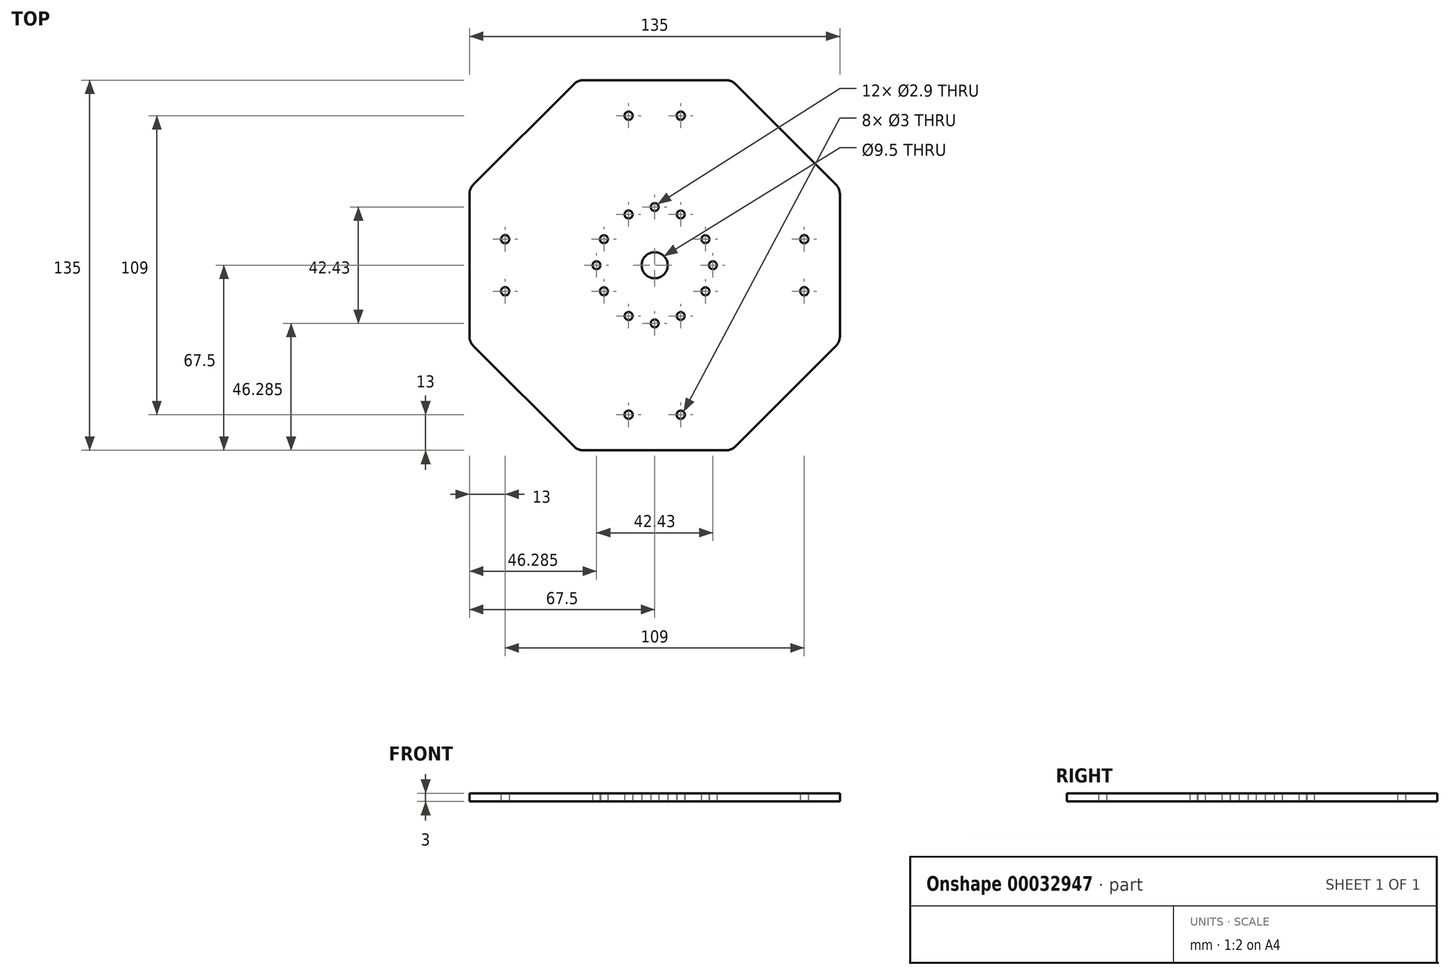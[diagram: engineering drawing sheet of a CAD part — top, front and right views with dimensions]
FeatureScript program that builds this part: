
annotation { "Feature Type Name" : "Feature", "Feature Type Description" : "" }
export const myFeature = defineFeature(function(context is Context, id is Id, definition is map)
    precondition{}
    {
        {
            var Q0;
            Q0=qCreatedBy(makeId("Top.planeOp"),FACE);
            var sketch = newSketch(context, id + "F0", { "sketchPlane" : qUnion([Q0])});
            skPoint(sketch, "E0.rect.middle", {"position": v(0, 0) * mm});
            skLineSegment(sketch, "E1", {"start": v(0, 67.5) * mm, "end": v(0, -67.5) * mm, "construction": true});
            skLineSegment(sketch, "E2", {"start": v(-67.5, 0) * mm, "end": v(67.5, 0) * mm, "construction": true});
            skLineSegment(sketch, "E3.rect.bottom", {"start": v(14, -14) * mm, "end": v(-14, -14) * mm, "construction": true});
            skLineSegment(sketch, "E3.rect.top", {"start": v(14, 14) * mm, "end": v(-14, 14) * mm, "construction": true});
            skLineSegment(sketch, "E3.rect.left", {"start": v(14, -14) * mm, "end": v(14, 14) * mm, "construction": true});
            skLineSegment(sketch, "E3.rect.right", {"start": v(-14, -14) * mm, "end": v(-14, 14) * mm, "construction": true});
            skLineSegment(sketch, "E4.rect.bottom", {"start": v(5, -5) * mm, "end": v(-5, -5) * mm, "construction": true});
            skLineSegment(sketch, "E4.rect.top", {"start": v(5, 5) * mm, "end": v(-5, 5) * mm, "construction": true});
            skLineSegment(sketch, "E4.rect.left", {"start": v(5, -5) * mm, "end": v(5, 5) * mm, "construction": true});
            skLineSegment(sketch, "E4.rect.right", {"start": v(-5, -5) * mm, "end": v(-5, 5) * mm, "construction": true});
            skLineSegment(sketch, "E5.bottom", {"start": v(-14, 14) * mm, "end": v(14, 14) * mm, "construction": true});
            skLineSegment(sketch, "E5.top", {"start": v(-14, 23) * mm, "end": v(14, 23) * mm, "construction": true});
            skLineSegment(sketch, "E5.left", {"start": v(-14, 14) * mm, "end": v(-14, 23) * mm, "construction": true});
            skLineSegment(sketch, "E5.right", {"start": v(14, 14) * mm, "end": v(14, 23) * mm, "construction": true});
            skLineSegment(sketch, "E6", {"start": v(5, 23) * mm, "end": v(5, 14) * mm, "construction": true});
            skLineSegment(sketch, "E7", {"start": v(14, 18.5) * mm, "end": v(5, 18.5) * mm, "construction": true});
            skCircle(sketch, "E8", {"center": v(9.5, 18.5) * mm, "radius": 1.45 * mm});
            skCircle(sketch, "E9.MirrorC", {"center": v(-9.5, 18.5) * mm, "radius": 1.45 * mm});
            skCircle(sketch, "E10.MirrorC", {"center": v(-9.5, -18.5) * mm, "radius": 1.45 * mm});
            skCircle(sketch, "E11.MirrorC", {"center": v(9.5, -18.5) * mm, "radius": 1.45 * mm});
            skCircle(sketch, "E12", {"center": v(0, 0) * mm, "radius": 20.8 * mm, "construction": true});
            skLineSegment(sketch, "E13", {"start": v(0, 0) * mm, "end": v(14, 14) * mm, "construction": true});
            skCircle(sketch, "E14.MirrorC", {"center": v(18.5, -9.5) * mm, "radius": 1.45 * mm});
            skCircle(sketch, "E15.MirrorC", {"center": v(18.5, 9.5) * mm, "radius": 1.45 * mm});
            skLineSegment(sketch, "E16", {"start": v(0, 0) * mm, "end": v(-14, 14) * mm, "construction": true});
            skCircle(sketch, "E17.MirrorC", {"center": v(-18.5, 9.5) * mm, "radius": 1.45 * mm});
            skCircle(sketch, "E18.MirrorC", {"center": v(-18.5, -9.5) * mm, "radius": 1.45 * mm});
            skCircle(sketch, "E19", {"center": v(9.5, 54.5) * mm, "radius": 1.5 * mm});
            skCircle(sketch, "E20.MirrorC", {"center": v(-9.5, 54.5) * mm, "radius": 1.5 * mm});
            skCircle(sketch, "E21.MirrorC", {"center": v(-9.5, -54.5) * mm, "radius": 1.5 * mm});
            skCircle(sketch, "E22.MirrorC", {"center": v(9.5, -54.5) * mm, "radius": 1.5 * mm});
            skCircle(sketch, "E23.MirrorC", {"center": v(54.5, -9.5) * mm, "radius": 1.5 * mm});
            skCircle(sketch, "E24.MirrorC", {"center": v(54.5, 9.5) * mm, "radius": 1.5 * mm});
            skCircle(sketch, "E25.MirrorC", {"center": v(-54.5, -9.5) * mm, "radius": 1.5 * mm});
            skCircle(sketch, "E26.MirrorC", {"center": v(-54.5, 9.5) * mm, "radius": 1.5 * mm});
            skLineSegment(sketch, "E27", {"start": v(0, 0) * mm, "end": v(95.46, 0) * mm, "construction": true});
            skLineSegment(sketch, "E28.MirrorCS", {"start": v(0, 0) * mm, "end": v(0, 95.46) * mm, "construction": true});
            skLineSegment(sketch, "E29", {"start": v(27.96, 67.5) * mm, "end": v(67.5, 27.96) * mm});
            skLineSegment(sketch, "E30.MirrorCS", {"start": v(-67.5, -27.96) * mm, "end": v(-27.96, -67.5) * mm});
            skLineSegment(sketch, "E31.MirrorCS", {"start": v(-27.96, 67.5) * mm, "end": v(-67.5, 27.96) * mm});
            skLineSegment(sketch, "E32.MirrorCS", {"start": v(27.96, -67.5) * mm, "end": v(67.5, -27.96) * mm});
            skLineSegment(sketch, "E33", {"start": v(67.5, -27.96) * mm, "end": v(67.5, 27.96) * mm});
            skLineSegment(sketch, "E34.MirrorCS", {"start": v(-67.5, -27.96) * mm, "end": v(-67.5, 27.96) * mm});
            skLineSegment(sketch, "E35.MirrorCS", {"start": v(-27.96, 67.5) * mm, "end": v(27.96, 67.5) * mm});
            skLineSegment(sketch, "E36.MirrorCS", {"start": v(27.96, -67.5) * mm, "end": v(-27.96, -67.5) * mm});
            skPoint(sketch, "E37.orphan", {"position": v(0, 95.46) * mm});
            skPoint(sketch, "E38.orphan", {"position": v(95.46, 0) * mm});
            skPoint(sketch, "E39.orphan", {"position": v(0, -95.46) * mm});
            skPoint(sketch, "E40.orphan", {"position": v(-95.46, 0) * mm});
            skCircle(sketch, "E41", {"center": v(0, 0) * mm, "radius": 4.75 * mm});
            skCircle(sketch, "E42", {"center": v(0, 21.21) * mm, "radius": 1.45 * mm});
            skCircle(sketch, "E43.1.0", {"center": v(-21.21, 0) * mm, "radius": 1.45 * mm});
            skCircle(sketch, "E43.2.0", {"center": v(0, -21.21) * mm, "radius": 1.45 * mm});
            skCircle(sketch, "E43.3.0", {"center": v(21.21, 0) * mm, "radius": 1.45 * mm});
            skSolve(sketch);
        }
        {
            var Q0;
            Q0=qSketchRegion(id+"F0",true);
            extrude(context, id + "F1", {"entities" : qUnion([Q0]), "depth" : 3 * mm});
        }
        {
            var Q0;
            Q0=makeQuery(id+"F1.opExtrude","SWEPT_EDGE",EDGE,{"disambiguationData":[OSD([sQuery(id+"F0.wireOp",EDGE,"E31.MirrorCS"),sQuery(id+"F0.wireOp",EDGE,"E35.MirrorCS")])]});
            var Q1;
            Q1=makeQuery(id+"F1.opExtrude","SWEPT_EDGE",EDGE,{"disambiguationData":[OSD([sQuery(id+"F0.wireOp",EDGE,"E31.MirrorCS"),sQuery(id+"F0.wireOp",EDGE,"E34.MirrorCS")])]});
            var Q2;
            Q2=makeQuery(id+"F1.opExtrude","SWEPT_EDGE",EDGE,{"disambiguationData":[OSD([sQuery(id+"F0.wireOp",EDGE,"E30.MirrorCS"),sQuery(id+"F0.wireOp",EDGE,"E34.MirrorCS")])]});
            var Q3;
            Q3=makeQuery(id+"F1.opExtrude","SWEPT_EDGE",EDGE,{"disambiguationData":[OSD([sQuery(id+"F0.wireOp",EDGE,"E30.MirrorCS"),sQuery(id+"F0.wireOp",EDGE,"E36.MirrorCS")])]});
            var Q4;
            Q4=makeQuery(id+"F1.opExtrude","SWEPT_EDGE",EDGE,{"disambiguationData":[OSD([sQuery(id+"F0.wireOp",EDGE,"E32.MirrorCS"),sQuery(id+"F0.wireOp",EDGE,"E36.MirrorCS")])]});
            var Q5;
            Q5=makeQuery(id+"F1.opExtrude","SWEPT_EDGE",EDGE,{"disambiguationData":[OSD([sQuery(id+"F0.wireOp",EDGE,"E32.MirrorCS"),sQuery(id+"F0.wireOp",EDGE,"E33")])]});
            var Q6;
            Q6=makeQuery(id+"F1.opExtrude","SWEPT_EDGE",EDGE,{"disambiguationData":[OSD([sQuery(id+"F0.wireOp",EDGE,"E29"),sQuery(id+"F0.wireOp",EDGE,"E33")])]});
            var Q7;
            Q7=makeQuery(id+"F1.opExtrude","SWEPT_EDGE",EDGE,{"disambiguationData":[OSD([sQuery(id+"F0.wireOp",EDGE,"E29"),sQuery(id+"F0.wireOp",EDGE,"E35.MirrorCS")])]});
            fillet(context, id + "F2", {"entities" : qUnion([Q0, Q1, Q2, Q3, Q4, Q5, Q6, Q7]), "radius" : 5 * mm, "tangentPropagation" : true, "allowEdgeOverflow" : false});
        }
    });
